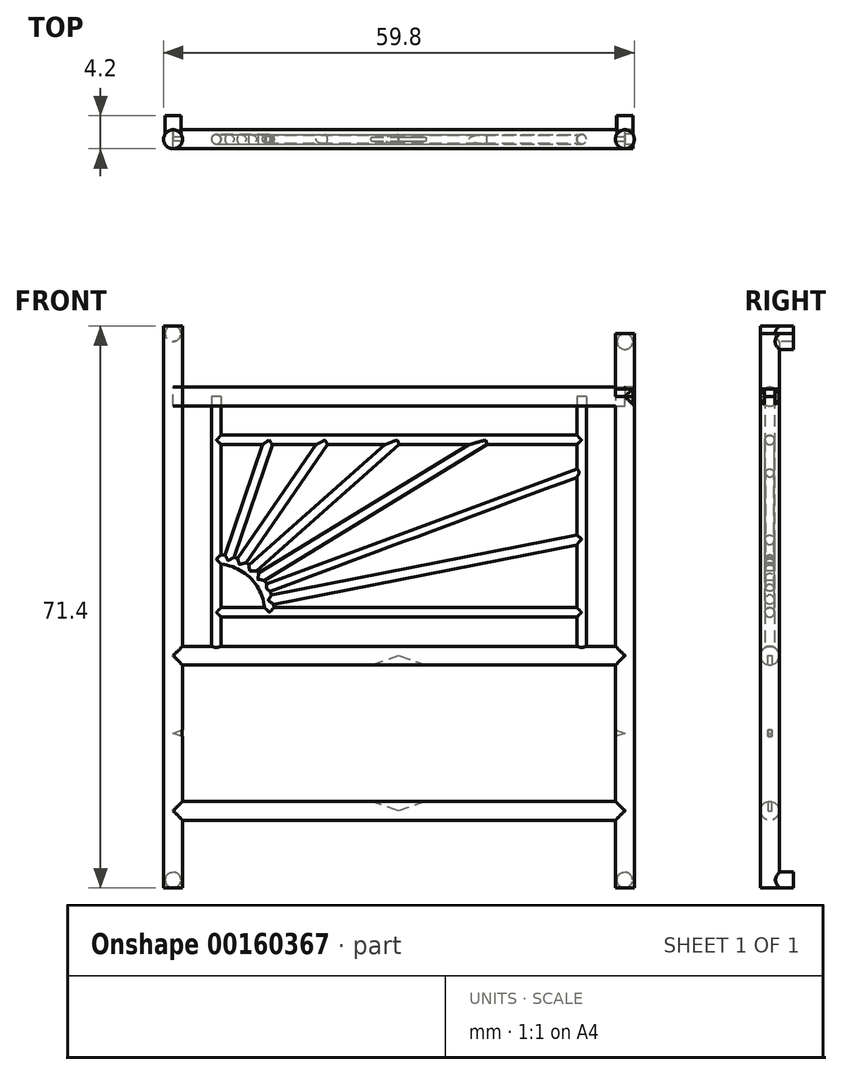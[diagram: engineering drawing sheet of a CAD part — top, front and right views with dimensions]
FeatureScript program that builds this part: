
annotation { "Feature Type Name" : "Feature", "Feature Type Description" : "" }
export const myFeature = defineFeature(function(context is Context, id is Id, definition is map)
    precondition{}
    {
        {
            var Q0;
            Q0=qCreatedBy(makeId("Right.planeOp"),FACE);
            cPlane(context, id + "F0", {"entities" : qUnion([Q0]), "cplaneType" : CPlaneType.OFFSET, "offset" : 57.4 * mm, "width" : 150 * mm, "height" : 150 * mm});
        }
        {
            var Q0;
            Q0=qCreatedBy(makeId("Top.planeOp"),FACE);
            cPlane(context, id + "F1", {"entities" : qUnion([Q0]), "cplaneType" : CPlaneType.OFFSET, "offset" : 4 * mm, "width" : 150 * mm, "height" : 150 * mm});
        }
        {
            var Q0;
            Q0=qCreatedBy(makeId("Top.planeOp"),FACE);
            cPlane(context, id + "F2", {"entities" : qUnion([Q0]), "cplaneType" : CPlaneType.OFFSET, "offset" : 57.4 * mm, "oppositeDirection" : true, "width" : 150 * mm, "height" : 150 * mm});
        }
        {
            var Q0;
            Q0=qCreatedBy(makeId("Front.planeOp"),FACE);
            var sketch = newSketch(context, id + "F3", { "sketchPlane" : qUnion([Q0])});
            skLineSegment(sketch, "E0", {"start": v(0, -57.4) * mm, "end": v(0, 4) * mm});
            skSolve(sketch);
        }
        {
            var Q0;
            Q0=qCreatedBy(makeId("Front.planeOp"),FACE);
            var sketch = newSketch(context, id + "F4", { "sketchPlane" : qUnion([Q0])});
            skLineSegment(sketch, "E1", {"start": v(57.4, 0) * mm, "end": v(57.4, -57.4) * mm});
            skSolve(sketch);
        }
        {
            var Q0;
            Q0=qCreatedBy(makeId("Front.planeOp"),FACE);
            var sketch = newSketch(context, id + "F5", { "sketchPlane" : qUnion([Q0])});
            skLineSegment(sketch, "E2", {"start": v(0, 0) * mm, "end": v(57.4, 0) * mm});
            skSolve(sketch);
        }
        {
            var Q0;
            Q0=qCreatedBy(makeId("Top.planeOp"),FACE);
            cPlane(context, id + "F6", {"entities" : qUnion([Q0]), "cplaneType" : CPlaneType.OFFSET, "offset" : 32.9 * mm, "oppositeDirection" : true, "width" : 150 * mm, "height" : 150 * mm});
        }
        {
            var Q0;
            Q0=qCreatedBy(makeId("Top.planeOp"),FACE);
            cPlane(context, id + "F7", {"entities" : qUnion([Q0]), "cplaneType" : CPlaneType.OFFSET, "offset" : 52.6 * mm, "oppositeDirection" : true, "width" : 150 * mm, "height" : 150 * mm});
        }
        {
            var Q0;
            Q0=qCreatedBy(makeId("Front.planeOp"),FACE);
            var sketch = newSketch(context, id + "F8", { "sketchPlane" : qUnion([Q0])});
            skLineSegment(sketch, "E3", {"start": v(0, -32.9) * mm, "end": v(57.4, -32.9) * mm});
            skSolve(sketch);
        }
        {
            var Q0;
            Q0=qCreatedBy(makeId("Front.planeOp"),FACE);
            var sketch = newSketch(context, id + "F9", { "sketchPlane" : qUnion([Q0])});
            skLineSegment(sketch, "E4", {"start": v(0, -52.6) * mm, "end": v(57.4, -52.6) * mm});
            skSolve(sketch);
        }
        {
            var Q0;
            Q0=qCreatedBy(id+"F1.planeOp",FACE);
            var sketch = newSketch(context, id + "F10", { "sketchPlane" : qUnion([Q0])});
            skCircle(sketch, "E5", {"center": v(0, 0) * mm, "radius": 1.2 * mm});
            skSolve(sketch);
        }
        {
            var Q0;
            Q0=makeQuery(id+"F10.imprint","IMPRINT",FACE,{"disambiguationData":[TD([[makeQuery(id+"F10.imprint","IMPRINT",EDGE,{"derivedFrom":sQuery(id+"F10.wireOp",EDGE,"E5")}),1.0]])]});
            var Q1;
            Q1=sQuery(id+"F3.wireOp",EDGE,"E0");
            sweep(context, id + "F11", {"profiles" : qUnion([Q0]), "path" : qUnion([Q1])});
        }
        {
            var Q0;
            Q0=qCreatedBy(makeId("Top.planeOp"),FACE);
            var sketch = newSketch(context, id + "F12", { "sketchPlane" : qUnion([Q0])});
            skCircle(sketch, "E6", {"center": v(57.4, 0) * mm, "radius": 1.2 * mm});
            skSolve(sketch);
        }
        {
            var Q0;
            Q0=makeQuery(id+"F12.imprint","IMPRINT",FACE,{"disambiguationData":[TD([[makeQuery(id+"F12.imprint","IMPRINT",EDGE,{"derivedFrom":sQuery(id+"F12.wireOp",EDGE,"E6")}),1.0]])]});
            var Q1;
            Q1=sQuery(id+"F4.wireOp",EDGE,"E1");
            sweep(context, id + "F13", {"profiles" : qUnion([Q0]), "path" : qUnion([Q1])});
        }
        {
            var Q0;
            Q0=qCreatedBy(makeId("Right.planeOp"),FACE);
            var sketch = newSketch(context, id + "F14", { "sketchPlane" : qUnion([Q0])});
            skCircle(sketch, "E7", {"center": v(0, 0) * mm, "radius": 1.2 * mm});
            skSolve(sketch);
        }
        {
            var Q0;
            Q0=qCreatedBy(makeId("Right.planeOp"),FACE);
            var sketch = newSketch(context, id + "F15", { "sketchPlane" : qUnion([Q0])});
            skCircle(sketch, "E8", {"center": v(0, -32.9) * mm, "radius": 1.2 * mm});
            skSolve(sketch);
        }
        {
            var Q0;
            Q0=qCreatedBy(makeId("Right.planeOp"),FACE);
            var sketch = newSketch(context, id + "F16", { "sketchPlane" : qUnion([Q0])});
            skCircle(sketch, "E9", {"center": v(0, -52.6) * mm, "radius": 1.2 * mm});
            skSolve(sketch);
        }
        {
            var Q0;
            Q0 = qSketchRegion(id + "F16", true);
            var Q1;
            Q1=sQuery(id+"F9.wireOp",EDGE,"E4");
            sweep(context, id + "F17", {"profiles" : qUnion([Q0]), "path" : qUnion([Q1])});
        }
        {
            var Q0;
            Q0 = qSketchRegion(id + "F15", true);
            var Q1;
            Q1=sQuery(id+"F8.wireOp",EDGE,"E3");
            sweep(context, id + "F18", {"profiles" : qUnion([Q0]), "path" : qUnion([Q1])});
        }
        {
            var Q0;
            Q0 = qSketchRegion(id + "F14", true);
            var Q1;
            Q1=sQuery(id+"F5.wireOp",EDGE,"E2");
            sweep(context, id + "F19", {"profiles" : qUnion([Q0]), "path" : qUnion([Q1])});
        }
        {
            var Q0;
            Q0=makeQuery(id+"F19.opSweep","CAP_FACE",FACE,{"disambiguationData":[OSD([sQuery(id+"F5.wireOp",VERTEX,"E2.end"),sQuery(id+"F14.wireOp",EDGE,"E7")])],"isStart":false});
            extrude(context, id + "F20", {"entities" : qUnion([Q0]), "depth" : 1 * mm});
        }
        {
            var Q0;
            Q0=qCreatedBy(makeId("Front.planeOp"),FACE);
            var sketch = newSketch(context, id + "F21", { "sketchPlane" : qUnion([Q0])});
            skLineSegment(sketch, "E10", {"start": v(5.5, 0) * mm, "end": v(5.5, -32.88) * mm});
            skSolve(sketch);
        }
        {
            var Q0;
            Q0=qCreatedBy(makeId("Front.planeOp"),FACE);
            var sketch = newSketch(context, id + "F22", { "sketchPlane" : qUnion([Q0])});
            skLineSegment(sketch, "E11", {"start": v(51.9, 0) * mm, "end": v(51.9, -32.9) * mm});
            skSolve(sketch);
        }
        {
            var Q0;
            Q0=qCreatedBy(makeId("Front.planeOp"),FACE);
            var sketch = newSketch(context, id + "F23", { "sketchPlane" : qUnion([Q0])});
            skLineSegment(sketch, "E12", {"start": v(5.5, -5.5) * mm, "end": v(51.9, -5.5) * mm});
            skSolve(sketch);
        }
        {
            var Q0;
            Q0=qCreatedBy(makeId("Front.planeOp"),FACE);
            var sketch = newSketch(context, id + "F24", { "sketchPlane" : qUnion([Q0])});
            skLineSegment(sketch, "E13", {"start": v(5.5, -27.4) * mm, "end": v(51.9, -27.4) * mm});
            skSolve(sketch);
        }
        {
            var Q0;
            Q0=qCreatedBy(makeId("Top.planeOp"),FACE);
            var sketch = newSketch(context, id + "F25", { "sketchPlane" : qUnion([Q0])});
            skCircle(sketch, "E14", {"center": v(5.5, 0) * mm, "radius": 0.6 * mm});
            skSolve(sketch);
        }
        {
            var Q0;
            Q0 = qSketchRegion(id + "F25", true);
            var Q1;
            Q1=sQuery(id+"F21.wireOp",EDGE,"E10");
            sweep(context, id + "F26", {"profiles" : qUnion([Q0]), "path" : qUnion([Q1])});
        }
        {
            var Q0;
            Q0=qCreatedBy(makeId("Top.planeOp"),FACE);
            var sketch = newSketch(context, id + "F27", { "sketchPlane" : qUnion([Q0])});
            skCircle(sketch, "E15", {"center": v(51.9, 0) * mm, "radius": 0.6 * mm});
            skSolve(sketch);
        }
        {
            var Q0;
            Q0 = qSketchRegion(id + "F27", true);
            var Q1;
            Q1=sQuery(id+"F22.wireOp",EDGE,"E11");
            sweep(context, id + "F28", {"profiles" : qUnion([Q0]), "path" : qUnion([Q1])});
        }
        {
            var Q0;
            Q0=makeQuery(id+"F13.opSweep","CAP_FACE",FACE,{"disambiguationData":[OSD([sQuery(id+"F4.wireOp",VERTEX,"E1.start"),sQuery(id+"F12.wireOp",EDGE,"E6")])],"isStart":true});
            extrude(context, id + "F29", {"entities" : qUnion([Q0]), "depth" : 1 * mm});
        }
        {
            var Q0;
            Q0=qCreatedBy(makeId("Right.planeOp"),FACE);
            var Q1;
            Q1=makeQuery(id+"F26.opSweep","SWEPT_FACE",FACE,{"disambiguationData":[OSD([sQuery(id+"F21.wireOp",EDGE,"E10"),sQuery(id+"F25.wireOp",EDGE,"E14")])]});
            cPlane(context, id + "F30", {"entities" : qUnion([Q0, Q1]), "cplaneType" : CPlaneType.LINE_ANGLE, "offset" : 25 * mm, "angle" : 0 * degree, "width" : 150 * mm, "height" : 150 * mm});
        }
        {
            var Q0;
            Q0=qCreatedBy(id+"F30.planeOp",FACE);
            var sketch = newSketch(context, id + "F31", { "sketchPlane" : qUnion([Q0])});
            skCircle(sketch, "E16", {"center": v(0, -5.5) * mm, "radius": 0.6 * mm});
            skSolve(sketch);
        }
        {
            var Q0;
            Q0=qCreatedBy(id+"F30.planeOp",FACE);
            var sketch = newSketch(context, id + "F32", { "sketchPlane" : qUnion([Q0])});
            skCircle(sketch, "E17", {"center": v(0, -27.4) * mm, "radius": 0.6 * mm});
            skSolve(sketch);
        }
        {
            var Q0;
            Q0 = qSketchRegion(id + "F31", true);
            var Q1;
            Q1=sQuery(id+"F23.wireOp",EDGE,"E12");
            sweep(context, id + "F33", {"profiles" : qUnion([Q0]), "path" : qUnion([Q1])});
        }
        {
            var Q0;
            Q0 = qSketchRegion(id + "F32", true);
            var Q1;
            Q1=sQuery(id+"F24.wireOp",EDGE,"E13");
            sweep(context, id + "F34", {"profiles" : qUnion([Q0]), "path" : qUnion([Q1])});
        }
        {
            var Q0;
            Q0=makeQuery(id+"F11.opSweep","SWEPT_BODY",BODY,{"disambiguationData":[OSD([sQuery(id+"F3.wireOp",EDGE,"E0"),sQuery(id+"F10.wireOp",EDGE,"E5")])]});
            var Q1;
            Q1=makeQuery(id+"F13.opSweep","SWEPT_BODY",BODY,{"disambiguationData":[OSD([sQuery(id+"F4.wireOp",EDGE,"E1"),sQuery(id+"F12.wireOp",EDGE,"E6")])]});
            var Q2;
            Q2=makeQuery(id+"F17.opSweep","SWEPT_BODY",BODY,{"disambiguationData":[OSD([sQuery(id+"F9.wireOp",EDGE,"E4"),sQuery(id+"F16.wireOp",EDGE,"E9")])]});
            var Q3;
            Q3=makeQuery(id+"F20.opExtrude","SWEPT_BODY",BODY,{"disambiguationData":[OSD([sQuery(id+"F5.wireOp",VERTEX,"E2.end"),sQuery(id+"F14.wireOp",EDGE,"E7")])]});
            var Q4;
            Q4=makeQuery(id+"F28.opSweep","SWEPT_BODY",BODY,{"disambiguationData":[OSD([sQuery(id+"F22.wireOp",EDGE,"E11"),sQuery(id+"F27.wireOp",EDGE,"E15")])]});
            var Q5;
            Q5=makeQuery(id+"F29.opExtrude","SWEPT_BODY",BODY,{"disambiguationData":[OSD([sQuery(id+"F4.wireOp",VERTEX,"E1.start"),sQuery(id+"F12.wireOp",EDGE,"E6")])]});
            var Q6;
            Q6=makeQuery(id+"F34.opSweep","SWEPT_BODY",BODY,{"disambiguationData":[OSD([sQuery(id+"F24.wireOp",EDGE,"E13"),sQuery(id+"F32.wireOp",EDGE,"E17")])]});
            booleanBodies(context, id + "F35", {"operationType" : BooleanOperationType.UNION, "tools" : qUnion([Q0, Q1, Q2, Q3, Q4, Q5, Q6])});
        }
        {
            var Q0;
            Q0=makeQuery(id+"F11.opSweep","SWEPT_BODY",BODY,{"disambiguationData":[OSD([sQuery(id+"F3.wireOp",EDGE,"E0"),sQuery(id+"F10.wireOp",EDGE,"E5")])]});
            var Q1;
            Q1=makeQuery(id+"F18.opSweep","SWEPT_BODY",BODY,{"disambiguationData":[OSD([sQuery(id+"F8.wireOp",EDGE,"E3"),sQuery(id+"F15.wireOp",EDGE,"E8")])]});
            var Q2;
            Q2=makeQuery(id+"F28.opSweep","SWEPT_BODY",BODY,{"disambiguationData":[OSD([sQuery(id+"F22.wireOp",EDGE,"E11"),sQuery(id+"F27.wireOp",EDGE,"E15")])]});
            booleanBodies(context, id + "F36", {"operationType" : BooleanOperationType.UNION, "tools" : qUnion([Q0, Q1, Q2])});
        }
        {
            var Q0;
            Q0=qCreatedBy(makeId("Front.planeOp"),FACE);
            var sketch = newSketch(context, id + "F37", { "sketchPlane" : qUnion([Q0])});
            skLineSegment(sketch, "E18", {"start": v(7, -20.82) * mm, "end": v(12.2, -5.5) * mm});
            skLineSegment(sketch, "E19", {"start": v(8.42, -21.32) * mm, "end": v(19.31, -5.5) * mm});
            skLineSegment(sketch, "E20", {"start": v(9.7, -22.12) * mm, "end": v(28.5, -5.5) * mm});
            skLineSegment(sketch, "E21", {"start": v(10.77, -23.19) * mm, "end": v(39.73, -5.5) * mm});
            skLineSegment(sketch, "E22", {"start": v(11.57, -24.47) * mm, "end": v(51.9, -9.49) * mm});
            skArc(sketch, "E23", {"start": v(12.24, -27.4) * mm, "mid": v(10.27, -22.63) * mm, "end": v(5.5, -20.65) * mm});
            skLineSegment(sketch, "E24", {"start": v(5.5, -27.4) * mm, "end": v(5.5, -26.72) * mm});
            skLineSegment(sketch, "E25", {"start": v(5.5, -27.4) * mm, "end": v(7, -20.82) * mm});
            skLineSegment(sketch, "E26", {"start": v(5.5, -27.4) * mm, "end": v(8.42, -21.32) * mm});
            skLineSegment(sketch, "E27", {"start": v(5.5, -27.4) * mm, "end": v(9.7, -22.12) * mm});
            skLineSegment(sketch, "E28", {"start": v(5.5, -27.4) * mm, "end": v(10.77, -23.19) * mm});
            skLineSegment(sketch, "E29", {"start": v(5.5, -27.4) * mm, "end": v(11.57, -24.47) * mm});
            skLineSegment(sketch, "E30", {"start": v(5.5, -27.4) * mm, "end": v(12.07, -25.9) * mm});
            skLineSegment(sketch, "E31", {"start": v(12.07, -25.9) * mm, "end": v(51.9, -18.08) * mm});
            skSolve(sketch);
        }
        {
            var Q0;
            Q0=qCreatedBy(id+"F30.planeOp",FACE);
            var sketch = newSketch(context, id + "F38", { "sketchPlane" : qUnion([Q0])});
            skCircle(sketch, "E32", {"center": v(0, -20.65) * mm, "radius": 0.6 * mm});
            skSolve(sketch);
        }
        {
            var Q0;
            Q0 = qSketchRegion(id + "F38", true);
            var Q1;
            Q1=sQuery(id+"F37.wireOp",EDGE,"I0ETbJWQ-2qSm-9uo4-h9Lq-IWVP6J6Rg5DC");
            var Q2;
            Q2=sQuery(id+"F37.wireOp",EDGE,"E23");
            sweep(context, id + "F39", {"operationType" : NewBodyOperationType.ADD, "profiles" : qUnion([Q0]), "path" : qUnion([Q1, Q2])});
        }
        {
            var Q0;
            Q0=makeQuery(id+"F11.opSweep","CAP_FACE",FACE,{"disambiguationData":[OSD([sQuery(id+"F3.wireOp",VERTEX,"E0.end"),sQuery(id+"F10.wireOp",EDGE,"E5")])],"isStart":true});
            extrude(context, id + "F40", {"entities" : qUnion([Q0]), "operationType" : NewBodyOperationType.ADD, "depth" : 5 * mm});
        }
        {
            var Q0;
            Q0=makeQuery(id+"F11.opSweep","CAP_FACE",FACE,{"disambiguationData":[OSD([sQuery(id+"F3.wireOp",VERTEX,"E0.start"),sQuery(id+"F10.wireOp",EDGE,"E5")])],"isStart":false});
            var Q1;
            Q1=makeQuery(id+"F11.opSweep","CAP_FACE",FACE,{"disambiguationData":[OSD([sQuery(id+"F3.wireOp",VERTEX,"E0.start"),sQuery(id+"F10.wireOp",EDGE,"E5")])],"isStart":false});
            extrude(context, id + "F41", {"entities" : qUnion([Q0, Q1]), "operationType" : NewBodyOperationType.ADD, "depth" : 5 * mm});
        }
        {
            var Q0;
            Q0=makeQuery(id+"F13.opSweep","CAP_FACE",FACE,{"disambiguationData":[OSD([sQuery(id+"F4.wireOp",VERTEX,"E1.end"),sQuery(id+"F12.wireOp",EDGE,"E6")])],"isStart":false});
            extrude(context, id + "F42", {"entities" : qUnion([Q0]), "operationType" : NewBodyOperationType.ADD, "depth" : 5 * mm});
        }
        {
            var Q0;
            Q0 = qSketchRegion(id + "F12", true);
            extrude(context, id + "F43", {"entities" : qUnion([Q0]), "depth" : 8 * mm});
        }
        {
            var Q0;
            Q0=qCreatedBy(makeId("Front.planeOp"),FACE);
            var sketch = newSketch(context, id + "F44", { "sketchPlane" : qUnion([Q0])});
            skCircle(sketch, "E33", {"center": v(0, -61.4) * mm, "radius": 1 * mm});
            skCircle(sketch, "E34", {"center": v(57.35, -61.4) * mm, "radius": 1 * mm});
            skCircle(sketch, "E35", {"center": v(0, 8) * mm, "radius": 1 * mm});
            skCircle(sketch, "E36", {"center": v(57.4, 7) * mm, "radius": 1 * mm});
            skSolve(sketch);
        }
        {
            var Q0;
            Q0 = qSketchRegion(id + "F44", true);
            extrude(context, id + "F45", {"entities" : qUnion([Q0]), "operationType" : NewBodyOperationType.ADD, "oppositeDirection" : true, "depth" : 3 * mm});
        }
        {
            var Q0;
            Q0=sQuery(id+"F37.wireOp",VERTEX,"E18.start");
            var Q1;
            Q1=sQuery(id+"F37.wireOp",EDGE,"E18");
            cPlane(context, id + "F46", {"entities" : qUnion([Q0, Q1]), "cplaneType" : CPlaneType.LINE_POINT, "offset" : 25 * mm, "width" : 150 * mm, "height" : 150 * mm});
        }
        {
            var Q0;
            Q0=qCreatedBy(id+"F46.planeOp",FACE);
            var sketch = newSketch(context, id + "F47", { "sketchPlane" : qUnion([Q0])});
            skCircle(sketch, "E37", {"center": v(13.32, 0) * mm, "radius": 0.6 * mm});
            skSolve(sketch);
        }
        {
            var Q0;
            Q0 = qSketchRegion(id + "F47", true);
            var Q1;
            Q1=sQuery(id+"F37.wireOp",EDGE,"E18");
            sweep(context, id + "F48", {"operationType" : NewBodyOperationType.ADD, "profiles" : qUnion([Q0]), "path" : qUnion([Q1])});
        }
        {
            var Q0;
            Q0=sQuery(id+"F37.wireOp",VERTEX,"E19.start");
            var Q1;
            Q1=sQuery(id+"F37.wireOp",EDGE,"E19");
            cPlane(context, id + "F49", {"entities" : qUnion([Q0, Q1]), "cplaneType" : CPlaneType.LINE_POINT, "offset" : 25 * mm, "width" : 150 * mm, "height" : 150 * mm});
        }
        {
            var Q0;
            Q0=qCreatedBy(id+"F49.planeOp",FACE);
            var sketch = newSketch(context, id + "F50", { "sketchPlane" : qUnion([Q0])});
            skCircle(sketch, "E38", {"center": v(19.02, 0) * mm, "radius": 0.6 * mm});
            skSolve(sketch);
        }
        {
            var Q0;
            Q0 = qSketchRegion(id + "F50", true);
            var Q1;
            Q1=sQuery(id+"F37.wireOp",EDGE,"E19");
            sweep(context, id + "F51", {"operationType" : NewBodyOperationType.ADD, "profiles" : qUnion([Q0]), "path" : qUnion([Q1])});
        }
        {
            var Q0;
            Q0=sQuery(id+"F37.wireOp",VERTEX,"E20.start");
            var Q1;
            Q1=sQuery(id+"F37.wireOp",EDGE,"E20");
            cPlane(context, id + "F52", {"entities" : qUnion([Q0, Q1]), "cplaneType" : CPlaneType.LINE_POINT, "offset" : 25 * mm, "width" : 150 * mm, "height" : 150 * mm});
        }
        {
            var Q0;
            Q0=qCreatedBy(id+"F52.planeOp",FACE);
            var sketch = newSketch(context, id + "F53", { "sketchPlane" : qUnion([Q0])});
            skCircle(sketch, "E39", {"center": v(0, -23) * mm, "radius": 0.6 * mm});
            skSolve(sketch);
        }
        {
            var Q0;
            Q0 = qSketchRegion(id + "F53", true);
            var Q1;
            Q1=sQuery(id+"F37.wireOp",EDGE,"E20");
            sweep(context, id + "F54", {"operationType" : NewBodyOperationType.ADD, "profiles" : qUnion([Q0]), "path" : qUnion([Q1])});
        }
        {
            var Q0;
            Q0=sQuery(id+"F37.wireOp",VERTEX,"E21.start");
            var Q1;
            Q1=sQuery(id+"F37.wireOp",EDGE,"E21");
            cPlane(context, id + "F55", {"entities" : qUnion([Q0, Q1]), "cplaneType" : CPlaneType.LINE_POINT, "offset" : 25 * mm, "width" : 150 * mm, "height" : 150 * mm});
        }
        {
            var Q0;
            Q0=qCreatedBy(id+"F55.planeOp",FACE);
            var sketch = newSketch(context, id + "F56", { "sketchPlane" : qUnion([Q0])});
            skCircle(sketch, "E40", {"center": v(0, -25.4) * mm, "radius": 0.6 * mm});
            skSolve(sketch);
        }
        {
            var Q0;
            Q0 = qSketchRegion(id + "F56", true);
            var Q1;
            Q1=sQuery(id+"F37.wireOp",EDGE,"E21");
            sweep(context, id + "F57", {"operationType" : NewBodyOperationType.ADD, "profiles" : qUnion([Q0]), "path" : qUnion([Q1])});
        }
        {
            var Q0;
            Q0=sQuery(id+"F37.wireOp",VERTEX,"E22.start");
            var Q1;
            Q1=sQuery(id+"F37.wireOp",EDGE,"E22");
            cPlane(context, id + "F58", {"entities" : qUnion([Q0, Q1]), "cplaneType" : CPlaneType.LINE_POINT, "offset" : 25 * mm, "width" : 150 * mm, "height" : 150 * mm});
        }
        {
            var Q0;
            Q0=qCreatedBy(id+"F58.planeOp",FACE);
            var sketch = newSketch(context, id + "F59", { "sketchPlane" : qUnion([Q0])});
            skCircle(sketch, "E41", {"center": v(0, -26.97) * mm, "radius": 0.5 * mm});
            skSolve(sketch);
        }
        {
            var Q0;
            Q0 = qSketchRegion(id + "F59", true);
            var Q1;
            Q1=sQuery(id+"F37.wireOp",EDGE,"E22");
            sweep(context, id + "F60", {"operationType" : NewBodyOperationType.ADD, "profiles" : qUnion([Q0]), "path" : qUnion([Q1])});
        }
        {
            var Q0;
            Q0=sQuery(id+"F37.wireOp",VERTEX,"m64XxsPV-IcbX-cnq1-dtZJ-hZMfToylPxtk.start");
            var Q1;
            Q1=sQuery(id+"F37.wireOp",EDGE,"m64XxsPV-IcbX-cnq1-dtZJ-hZMfToylPxtk");
            var Q2;
            Q2=sQuery(id+"F37.wireOp",VERTEX,"E30.end");
            var Q3;
            Q3=sQuery(id+"F37.wireOp",EDGE,"E31");
            cPlane(context, id + "F61", {"entities" : qUnion([Q0, Q1, Q2, Q3]), "cplaneType" : CPlaneType.LINE_POINT, "offset" : 25 * mm, "width" : 150 * mm, "height" : 150 * mm});
        }
        {
            var Q0;
            Q0=qCreatedBy(id+"F61.planeOp",FACE);
            var sketch = newSketch(context, id + "F62", { "sketchPlane" : qUnion([Q0])});
            skCircle(sketch, "E42", {"center": v(0, -27.73) * mm, "radius": 0.6 * mm});
            skSolve(sketch);
        }
        {
            var Q0;
            Q0 = qSketchRegion(id + "F62", true);
            var Q1;
            Q1=sQuery(id+"F37.wireOp",EDGE,"m64XxsPV-IcbX-cnq1-dtZJ-hZMfToylPxtk");
            var Q2;
            Q2=sQuery(id+"F37.wireOp",EDGE,"E31");
            sweep(context, id + "F63", {"operationType" : NewBodyOperationType.ADD, "profiles" : qUnion([Q0]), "path" : qUnion([Q1, Q2])});
        }
        {
            var Q0;
            Q0=qCreatedBy(makeId("Front.planeOp"),FACE);
            var sketch = newSketch(context, id + "F64", { "sketchPlane" : qUnion([Q0])});
            skLineSegment(sketch, "E43", {"start": v(0, -42.75) * mm, "end": v(28.66, -32.9) * mm});
            skLineSegment(sketch, "E44", {"start": v(28.65, -32.9) * mm, "end": v(57.4, -42.75) * mm});
            skLineSegment(sketch, "E45", {"start": v(57.4, -42.75) * mm, "end": v(28.66, -52.6) * mm});
            skLineSegment(sketch, "E46", {"start": v(28.66, -52.6) * mm, "end": v(0, -42.75) * mm});
            skSolve(sketch);
        }
        {
            var Q0;
            Q0=makeQuery(id+"F64.imprint","IMPRINT",FACE,{"disambiguationData":[TD([[makeQuery(id+"F64.imprint","IMPRINT",EDGE,{"derivedFrom":sQuery(id+"F64.wireOp",EDGE,"E43")}),-1.0]])]});
            extrude(context, id + "F65", {"entities" : qUnion([Q0]), "operationType" : NewBodyOperationType.REMOVE, "endBound" : BoundingType.SYMMETRIC, "depth" : 0.5 * mm});
        }
    });
